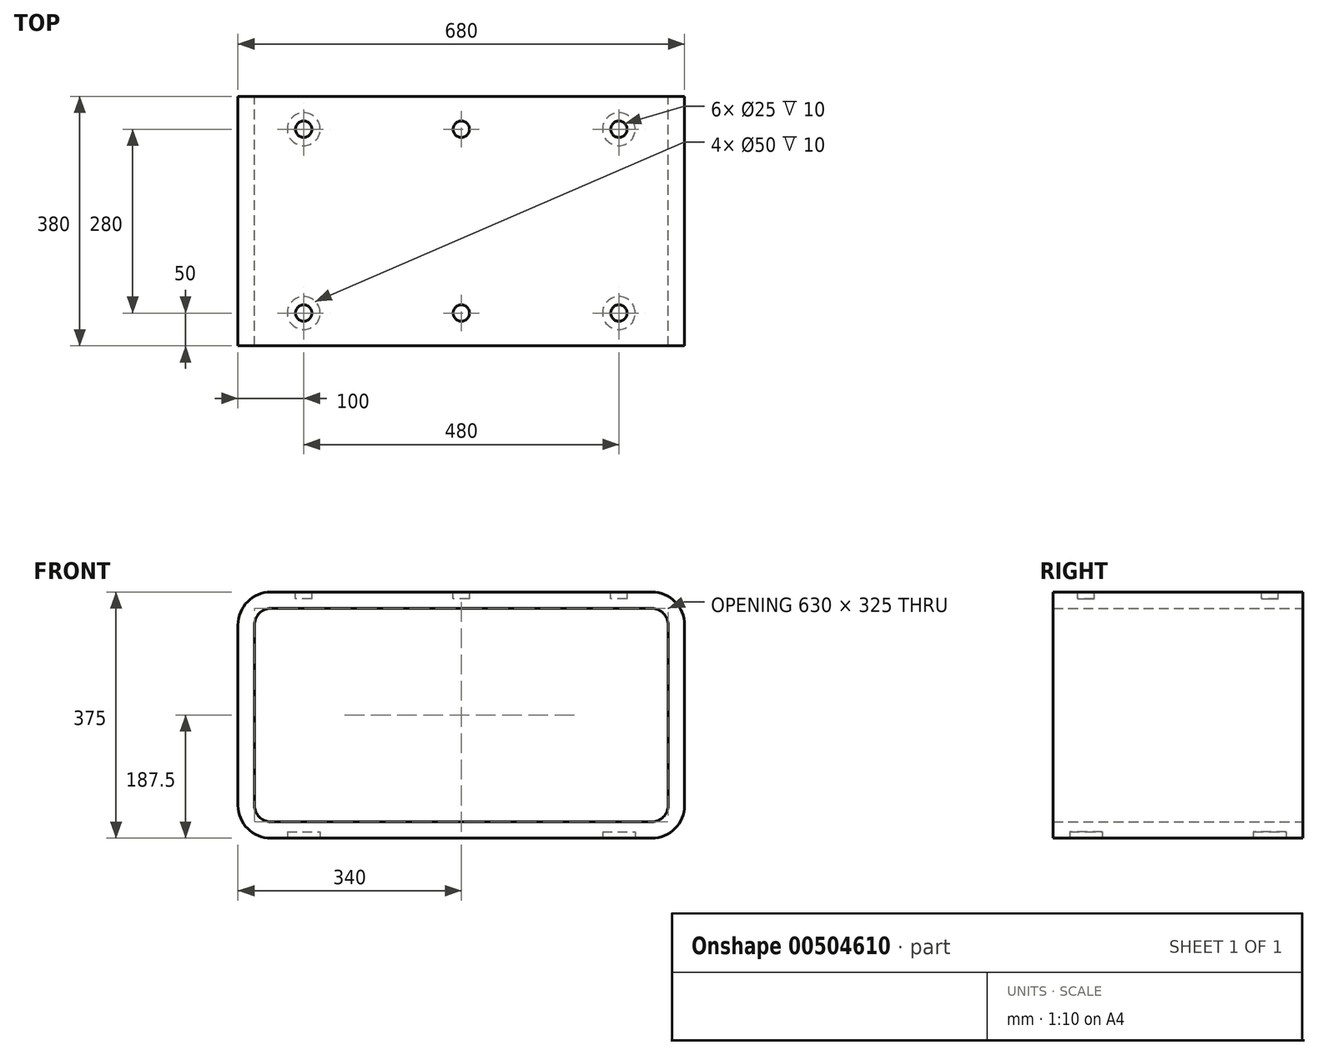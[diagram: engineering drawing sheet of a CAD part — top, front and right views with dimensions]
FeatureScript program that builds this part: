
annotation { "Feature Type Name" : "Feature", "Feature Type Description" : "" }
export const myFeature = defineFeature(function(context is Context, id is Id, definition is map)
    precondition{}
    {
        {
            var Q0;
            Q0=qCreatedBy(makeId("Front.planeOp"),FACE);
            var sketch = newSketch(context, id + "F0", { "sketchPlane" : qUnion([Q0])});
            skLineSegment(sketch, "E0.bottom", {"start": v(290, -187.5) * mm, "end": v(-290, -187.5) * mm});
            skLineSegment(sketch, "E0.top", {"start": v(290, 187.5) * mm, "end": v(-290, 187.5) * mm});
            skLineSegment(sketch, "E0.left", {"start": v(340, -137.5) * mm, "end": v(340, 137.5) * mm});
            skLineSegment(sketch, "E0.right", {"start": v(-340, -137.5) * mm, "end": v(-340, 137.5) * mm});
            skPoint(sketch, "E0.middle", {"position": v(0, 0) * mm});
            skPoint(sketch, "E1.visualSharp", {"position": v(-340, 187.5) * mm});
            skArc(sketch, "E1.filletArc", {"start": v(-290, 187.5) * mm, "mid": v(-325.36, 172.86) * mm, "end": v(-340, 137.5) * mm});
            skPoint(sketch, "E2.visualSharp", {"position": v(-340, -187.5) * mm});
            skArc(sketch, "E2.filletArc", {"start": v(-340, -137.5) * mm, "mid": v(-325.36, -172.86) * mm, "end": v(-290, -187.5) * mm});
            skPoint(sketch, "E3.visualSharp", {"position": v(340, -187.5) * mm});
            skArc(sketch, "E3.filletArc", {"start": v(290, -187.5) * mm, "mid": v(325.36, -172.86) * mm, "end": v(340, -137.5) * mm});
            skPoint(sketch, "E4.visualSharp", {"position": v(340, 187.5) * mm});
            skArc(sketch, "E4.filletArc", {"start": v(340, 137.5) * mm, "mid": v(325.36, 172.86) * mm, "end": v(290, 187.5) * mm});
            skArc(sketch, "E5.0", {"start": v(290, -162.5) * mm, "mid": v(307.68, -155.18) * mm, "end": v(315, -137.5) * mm});
            skLineSegment(sketch, "E5.1", {"start": v(315, -137.5) * mm, "end": v(315, 137.5) * mm});
            skLineSegment(sketch, "E5.2", {"start": v(290, -162.5) * mm, "end": v(-290, -162.5) * mm});
            skArc(sketch, "E5.3", {"start": v(315, 137.5) * mm, "mid": v(307.68, 155.18) * mm, "end": v(290, 162.5) * mm});
            skArc(sketch, "E5.4", {"start": v(-315, -137.5) * mm, "mid": v(-307.68, -155.18) * mm, "end": v(-290, -162.5) * mm});
            skLineSegment(sketch, "E5.5", {"start": v(-315, -137.5) * mm, "end": v(-315, 137.5) * mm});
            skArc(sketch, "E5.6", {"start": v(-290, 162.5) * mm, "mid": v(-307.68, 155.18) * mm, "end": v(-315, 137.5) * mm});
            skLineSegment(sketch, "E5.7", {"start": v(290, 162.5) * mm, "end": v(-290, 162.5) * mm});
            skSolve(sketch);
        }
        {
            var Q0;
            Q0=makeQuery(id+"F0.imprint","IMPRINT",FACE,{"disambiguationData":[TD([[makeQuery(id+"F0.imprint","IMPRINT",EDGE,{"derivedFrom":sQuery(id+"F0.wireOp",EDGE,"E0.bottom")}),-1.0]])]});
            extrude(context, id + "F1", {"entities" : qUnion([Q0]), "depth" : 380 * mm});
        }
        {
            var Q0;
            Q0=makeQuery(id+"F1.opExtrude","SWEPT_FACE",FACE,{"disambiguationData":[OSD([sQuery(id+"F0.wireOp",EDGE,"E0.bottom")])]});
            var sketch = newSketch(context, id + "F2", { "sketchPlane" : qUnion([Q0])});
            skCircle(sketch, "E6", {"center": v(-240, 330) * mm, "radius": 25 * mm});
            skCircle(sketch, "E7", {"center": v(-240, 50) * mm, "radius": 25 * mm});
            skCircle(sketch, "E8", {"center": v(240, 50) * mm, "radius": 25 * mm});
            skCircle(sketch, "E9", {"center": v(240, 330) * mm, "radius": 25 * mm});
            skSolve(sketch);
        }
        {
            var Q0;
            Q0=makeQuery(id+"F2.imprint","IMPRINT",FACE,{"disambiguationData":[TD([[makeQuery(id+"F2.imprint","IMPRINT",EDGE,{"derivedFrom":sQuery(id+"F2.wireOp",EDGE,"E6")}),1.0]])]});
            var Q1;
            Q1=makeQuery(id+"F2.imprint","IMPRINT",FACE,{"disambiguationData":[TD([[makeQuery(id+"F2.imprint","IMPRINT",EDGE,{"derivedFrom":sQuery(id+"F2.wireOp",EDGE,"E7")}),1.0]])]});
            var Q2;
            Q2=makeQuery(id+"F2.imprint","IMPRINT",FACE,{"disambiguationData":[TD([[makeQuery(id+"F2.imprint","IMPRINT",EDGE,{"derivedFrom":sQuery(id+"F2.wireOp",EDGE,"E8")}),1.0]])]});
            var Q3;
            Q3=makeQuery(id+"F2.imprint","IMPRINT",FACE,{"disambiguationData":[TD([[makeQuery(id+"F2.imprint","IMPRINT",EDGE,{"derivedFrom":sQuery(id+"F2.wireOp",EDGE,"E9")}),1.0]])]});
            extrude(context, id + "F3", {"entities" : qUnion([Q0, Q1, Q2, Q3]), "operationType" : NewBodyOperationType.REMOVE, "oppositeDirection" : true, "depth" : 10 * mm});
        }
        {
            var Q0;
            Q0=makeQuery(id+"F1.opExtrude","SWEPT_FACE",FACE,{"disambiguationData":[OSD([sQuery(id+"F0.wireOp",EDGE,"E0.top")])]});
            var sketch = newSketch(context, id + "F4", { "sketchPlane" : qUnion([Q0])});
            skCircle(sketch, "E10", {"center": v(-240, -50) * mm, "radius": 12.5 * mm});
            skCircle(sketch, "E11", {"center": v(-240, -330) * mm, "radius": 12.5 * mm});
            skCircle(sketch, "E12", {"center": v(240, -330) * mm, "radius": 12.5 * mm});
            skCircle(sketch, "E13", {"center": v(240, -50) * mm, "radius": 12.5 * mm});
            skCircle(sketch, "E14", {"center": v(0, -330) * mm, "radius": 12.5 * mm});
            skCircle(sketch, "E15", {"center": v(0, -50) * mm, "radius": 12.5 * mm});
            skSolve(sketch);
        }
        {
            var Q0;
            Q0=makeQuery(id+"F4.imprint","IMPRINT",FACE,{"disambiguationData":[TD([[makeQuery(id+"F4.imprint","IMPRINT",EDGE,{"derivedFrom":sQuery(id+"F4.wireOp",EDGE,"E11")}),1.0]])]});
            var Q1;
            Q1=makeQuery(id+"F4.imprint","IMPRINT",FACE,{"disambiguationData":[TD([[makeQuery(id+"F4.imprint","IMPRINT",EDGE,{"derivedFrom":sQuery(id+"F4.wireOp",EDGE,"E10")}),1.0]])]});
            var Q2;
            Q2=makeQuery(id+"F4.imprint","IMPRINT",FACE,{"disambiguationData":[TD([[makeQuery(id+"F4.imprint","IMPRINT",EDGE,{"derivedFrom":sQuery(id+"F4.wireOp",EDGE,"E14")}),1.0]])]});
            var Q3;
            Q3=makeQuery(id+"F4.imprint","IMPRINT",FACE,{"disambiguationData":[TD([[makeQuery(id+"F4.imprint","IMPRINT",EDGE,{"derivedFrom":sQuery(id+"F4.wireOp",EDGE,"E15")}),1.0]])]});
            var Q4;
            Q4=makeQuery(id+"F4.imprint","IMPRINT",FACE,{"disambiguationData":[TD([[makeQuery(id+"F4.imprint","IMPRINT",EDGE,{"derivedFrom":sQuery(id+"F4.wireOp",EDGE,"E12")}),1.0]])]});
            var Q5;
            Q5=makeQuery(id+"F4.imprint","IMPRINT",FACE,{"disambiguationData":[TD([[makeQuery(id+"F4.imprint","IMPRINT",EDGE,{"derivedFrom":sQuery(id+"F4.wireOp",EDGE,"E13")}),1.0]])]});
            extrude(context, id + "F5", {"entities" : qUnion([Q0, Q1, Q2, Q3, Q4, Q5]), "operationType" : NewBodyOperationType.REMOVE, "oppositeDirection" : true, "depth" : 10 * mm});
        }
    });
